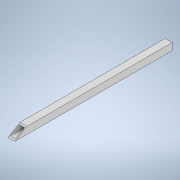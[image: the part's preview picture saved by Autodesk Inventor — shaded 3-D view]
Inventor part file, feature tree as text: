
AUTODESK INVENTOR PART (.ipt)
format: ipt  version: 2020.2 (Build 242310000, 310)  size: 117,248 bytes
history: native  units: in
note: dims shown in document units (in); Inventor stores cm internally (conversion verified against a paired STEP export)
features: extrude x2, sketch x2
ambient origin geometry x8: Origin, YZ Plane, XZ Plane, XY Plane, X Axis, Y Axis, Z Axis, Center Point
bodies: Solid1 (feature_tree)
feature tree (4):
  extrude  "Extrusion1"  Depth=1.0in
  extrude  "Extrusion2"  Depth=0.125in TaperAngle=0.0deg
  sketch  "Sketch1"  dims[d0=1.0in d1=1.0in]
  sketch  "Sketch2"  dims[d2=0.125in d3=22.375in d4=0.0in d5=30.0deg d6=0.0in d7=0.0in d8=0.5in d9=0.0344in]
